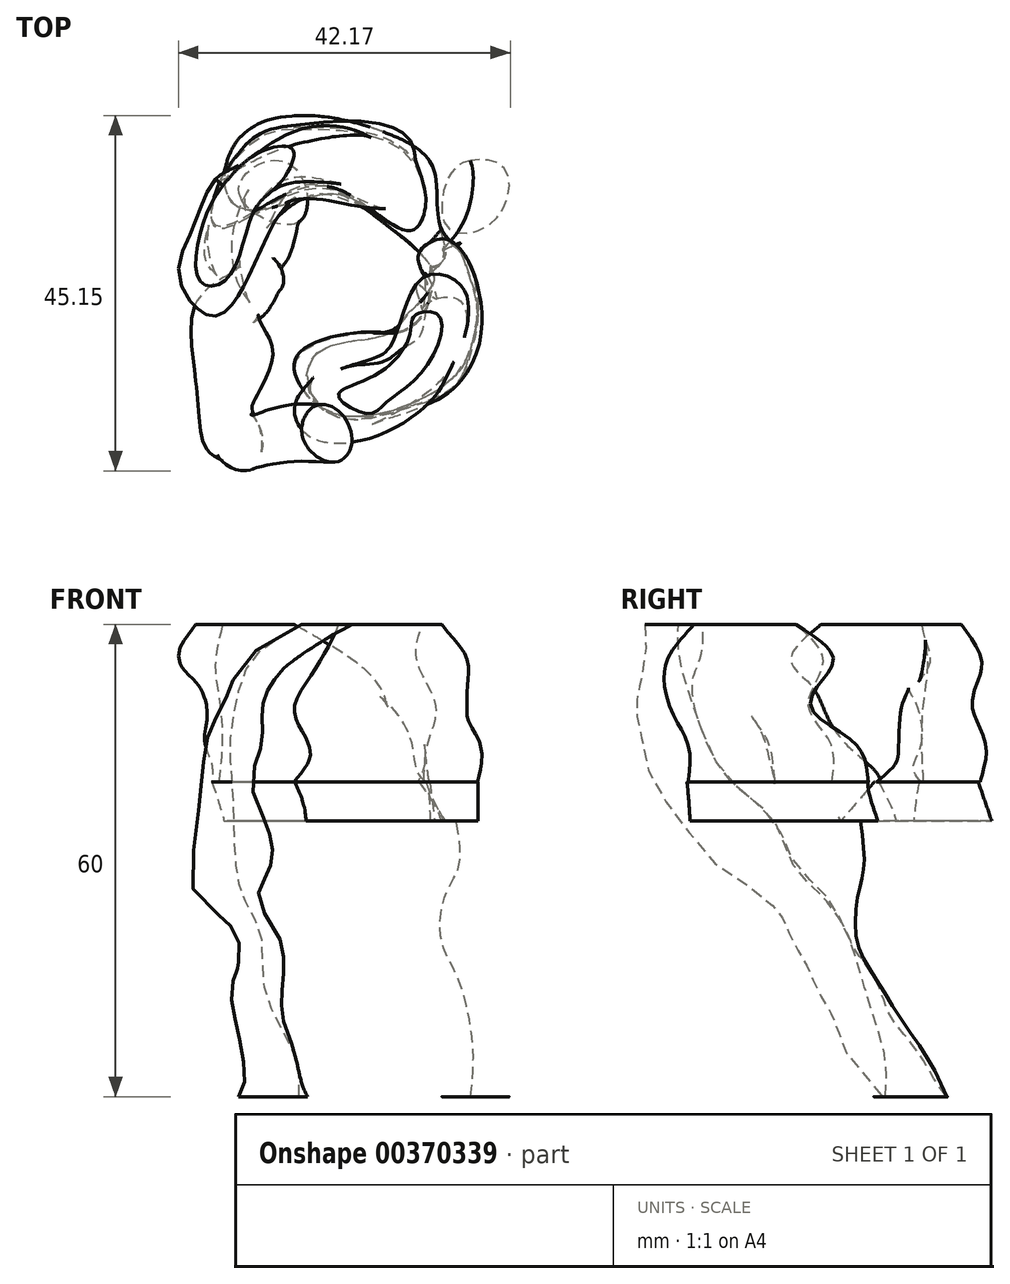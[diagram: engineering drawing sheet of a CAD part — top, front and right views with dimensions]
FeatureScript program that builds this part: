
annotation { "Feature Type Name" : "Feature", "Feature Type Description" : "" }
export const myFeature = defineFeature(function(context is Context, id is Id, definition is map)
    precondition{}
    {
        {
            var Q0;
            Q0=qCreatedBy(makeId("Top.planeOp"),FACE);
            cPlane(context, id + "F0", {"entities" : qUnion([Q0]), "cplaneType" : CPlaneType.OFFSET, "offset" : 5 * mm, "width" : 152.4 * mm, "height" : 152.4 * mm});
        }
        {
            var Q0;
            Q0=qCreatedBy(id+"F0.planeOp",FACE);
            var sketch = newSketch(context, id + "F1", { "sketchPlane" : qUnion([Q0])});
            skFitSpline(sketch, "E0", {"points": [v(-10.96, 11.92) * mm, v(-18.66, 15.77) * mm, v(-12.5, 19.43) * mm, v(-10.96, 11.92) * mm]});
            skSolve(sketch);
        }
        {
            var Q0;
            Q0=qCreatedBy(id+"F0.planeOp",FACE);
            var sketch = newSketch(context, id + "F2", { "sketchPlane" : qUnion([Q0])});
            skFitSpline(sketch, "E1", {"points": [v(10.8, 19.7) * mm, v(7.88, 17.32) * mm, v(7.93, 11.12) * mm, v(13.79, 12.03) * mm, v(15.2, 18.53) * mm, v(10.8, 19.7) * mm]});
            skSolve(sketch);
        }
        {
            var Q0;
            Q0=qCreatedBy(id+"F0.planeOp",FACE);
            cPlane(context, id + "F3", {"entities" : qUnion([Q0]), "cplaneType" : CPlaneType.OFFSET, "offset" : 5 * mm, "width" : 152.4 * mm, "height" : 152.4 * mm});
        }
        {
            var Q0;
            Q0=qCreatedBy(id+"F3.planeOp",FACE);
            var sketch = newSketch(context, id + "F4", { "sketchPlane" : qUnion([Q0])});
            skFitSpline(sketch, "E2", {"points": [v(-17.89, 12.12) * mm, v(-16.73, 16.35) * mm, v(-11.92, 13.66) * mm, v(-13.08, 7.3) * mm, v(-17.89, 12.12) * mm]});
            skSolve(sketch);
        }
        {
            var Q0;
            Q0=qCreatedBy(id+"F3.planeOp",FACE);
            var sketch = newSketch(context, id + "F5", { "sketchPlane" : qUnion([Q0])});
            skFitSpline(sketch, "E3", {"points": [v(13.6, 16.47) * mm, v(8.9, 16.15) * mm, v(7.47, 12.01) * mm, v(9.86, 7.3) * mm, v(14.84, 7.32) * mm, v(13.6, 16.47) * mm]});
            skSolve(sketch);
        }
        {
            var Q0;
            Q0=qCreatedBy(id+"F3.planeOp",FACE);
            cPlane(context, id + "F6", {"entities" : qUnion([Q0]), "cplaneType" : CPlaneType.OFFSET, "offset" : 5 * mm, "width" : 152.4 * mm, "height" : 152.4 * mm});
        }
        {
            var Q0;
            Q0=qCreatedBy(id+"F6.planeOp",FACE);
            var sketch = newSketch(context, id + "F7", { "sketchPlane" : qUnion([Q0])});
            skFitSpline(sketch, "E4", {"points": [v(-18.08, 9.04) * mm, v(-18.85, 12.3) * mm, v(-14.42, 11.16) * mm, v(-13.66, 5.39) * mm, v(-18.08, 9.04) * mm]});
            skSolve(sketch);
        }
        {
            var Q0;
            Q0=qCreatedBy(id+"F6.planeOp",FACE);
            var sketch = newSketch(context, id + "F8", { "sketchPlane" : qUnion([Q0])});
            skFitSpline(sketch, "E5", {"points": [v(10.24, 13.8) * mm, v(6.16, 10.54) * mm, v(7.66, 5.82) * mm, v(13.24, 4.66) * mm, v(13.5, 10.57) * mm, v(10.24, 13.8) * mm]});
            skSolve(sketch);
        }
        {
            var Q0;
            Q0=qCreatedBy(id+"F6.planeOp",FACE);
            cPlane(context, id + "F9", {"entities" : qUnion([Q0]), "cplaneType" : CPlaneType.OFFSET, "offset" : 5 * mm, "width" : 152.4 * mm, "height" : 152.4 * mm});
        }
        {
            var Q0;
            Q0=qCreatedBy(id+"F9.planeOp",FACE);
            var sketch = newSketch(context, id + "F10", { "sketchPlane" : qUnion([Q0])});
            skFitSpline(sketch, "E6", {"points": [v(-19.23, 7.7) * mm, v(-17.89, 10.58) * mm, v(-13.08, 3.85) * mm, v(-17.89, 3.27) * mm, v(-19.23, 7.7) * mm]});
            skSolve(sketch);
        }
        {
            var Q0;
            Q0=qCreatedBy(id+"F9.planeOp",FACE);
            var sketch = newSketch(context, id + "F11", { "sketchPlane" : qUnion([Q0])});
            skFitSpline(sketch, "E7", {"points": [v(8.32, 10.92) * mm, v(5.05, 8.14) * mm, v(7.28, 3.19) * mm, v(11.85, 3.4) * mm, v(12, 7.44) * mm, v(8.32, 10.92) * mm]});
            skSolve(sketch);
        }
        {
            var Q0;
            Q0=qCreatedBy(id+"F9.planeOp",FACE);
            cPlane(context, id + "F12", {"entities" : qUnion([Q0]), "cplaneType" : CPlaneType.OFFSET, "offset" : 5 * mm, "width" : 152.4 * mm, "height" : 152.4 * mm});
        }
        {
            var Q0;
            Q0=qCreatedBy(id+"F12.planeOp",FACE);
            var sketch = newSketch(context, id + "F13", { "sketchPlane" : qUnion([Q0])});
            skFitSpline(sketch, "E8", {"points": [v(-18.29, 6.81) * mm, v(-18.45, 4.24) * mm, v(-16.23, 0) * mm, v(-13.87, 2.6) * mm, v(-14.27, 6.83) * mm, v(-18.29, 6.81) * mm]});
            skSolve(sketch);
        }
        {
            var Q0;
            Q0=qCreatedBy(id+"F12.planeOp",FACE);
            var sketch = newSketch(context, id + "F14", { "sketchPlane" : qUnion([Q0])});
            skFitSpline(sketch, "E9", {"points": [v(7.64, 7.65) * mm, v(3.8, 9.66) * mm, v(0, 9.46) * mm, v(-2.02, 4.86) * mm, v(0, 0) * mm, v(9.54, 0) * mm, v(7.64, 7.65) * mm]});
            skSolve(sketch);
        }
        {
            var Q0;
            Q0=qCreatedBy(id+"F12.planeOp",FACE);
            cPlane(context, id + "F15", {"entities" : qUnion([Q0]), "cplaneType" : CPlaneType.OFFSET, "offset" : 5 * mm, "width" : 152.4 * mm, "height" : 152.4 * mm});
        }
        {
            var Q0;
            Q0=qCreatedBy(id+"F15.planeOp",FACE);
            var sketch = newSketch(context, id + "F16", { "sketchPlane" : qUnion([Q0])});
            skFitSpline(sketch, "E10", {"points": [v(-18.6, 4.65) * mm, v(-22.98, 2.98) * mm, v(-23.13, 0) * mm, v(-19.28, -3.26) * mm, v(-16.2, 0) * mm, v(-18.6, 4.65) * mm]});
            skSolve(sketch);
        }
        {
            var Q0;
            Q0=qCreatedBy(id+"F15.planeOp",FACE);
            var sketch = newSketch(context, id + "F17", { "sketchPlane" : qUnion([Q0])});
            skFitSpline(sketch, "E11", {"points": [v(7.68, 6.97) * mm, v(5.25, 13.94) * mm, v(-1.9, 16.67) * mm, v(-3.69, 12.07) * mm, v(-3.1, 6.74) * mm, v(0, -1.34) * mm, v(-2.44, -7.79) * mm, v(7.07, -8.48) * mm, v(9.93, 0) * mm, v(7.68, 6.97) * mm]});
            skSolve(sketch);
        }
        {
            var Q0;
            Q0=qCreatedBy(id+"F15.planeOp",FACE);
            cPlane(context, id + "F18", {"entities" : qUnion([Q0]), "cplaneType" : CPlaneType.OFFSET, "offset" : 5 * mm, "width" : 152.4 * mm, "height" : 152.4 * mm});
        }
        {
            var Q0;
            Q0=qCreatedBy(id+"F18.planeOp",FACE);
            var sketch = newSketch(context, id + "F19", { "sketchPlane" : qUnion([Q0])});
            skFitSpline(sketch, "E12", {"points": [v(-22.76, 0) * mm, v(-24.55, -3.05) * mm, v(-21.94, -10.02) * mm, v(-14.84, -5.95) * mm, v(-15.97, -1.54) * mm, v(-22.76, 0) * mm]});
            skSolve(sketch);
        }
        {
            var Q0;
            Q0=qCreatedBy(id+"F18.planeOp",FACE);
            var sketch = newSketch(context, id + "F20", { "sketchPlane" : qUnion([Q0])});
            skFitSpline(sketch, "E13", {"points": [v(3.97, 18.59) * mm, v(0, 21.33) * mm, v(-10.87, 23.3) * mm, v(-10.82, 17.6) * mm, v(-4.03, 12.67) * mm, v(0, 7.72) * mm, v(3.38, 0) * mm, v(0, -4.6) * mm, v(-5.9, -5.91) * mm, v(-8.42, -10.34) * mm, v(0, -12.51) * mm, v(10.7, -2.54) * mm, v(9.52, 9.05) * mm, v(3.97, 18.59) * mm]});
            skSolve(sketch);
        }
        {
            var Q0;
            Q0=qCreatedBy(id+"F18.planeOp",FACE);
            cPlane(context, id + "F21", {"entities" : qUnion([Q0]), "cplaneType" : CPlaneType.OFFSET, "offset" : 5 * mm, "width" : 152.4 * mm, "height" : 152.4 * mm});
        }
        {
            var Q0;
            Q0=qCreatedBy(id+"F21.planeOp",FACE);
            var sketch = newSketch(context, id + "F22", { "sketchPlane" : qUnion([Q0])});
            skFitSpline(sketch, "E14", {"points": [v(-21.05, -2.61) * mm, v(-23.57, -7.6) * mm, v(-22.98, -13.47) * mm, v(-18.96, -13.09) * mm, v(-15.36, -6.64) * mm, v(-17.95, -2.6) * mm, v(-21.05, -2.61) * mm]});
            skSolve(sketch);
        }
        {
            var Q0;
            Q0=qCreatedBy(id+"F21.planeOp",FACE);
            var sketch = newSketch(context, id + "F23", { "sketchPlane" : qUnion([Q0])});
            skFitSpline(sketch, "E15", {"points": [v(0, 23.21) * mm, v(-9.58, 25.38) * mm, v(-18.32, 22.77) * mm, v(-20.28, 15.78) * mm, v(-16.6, 13.4) * mm, v(-6.58, 15.47) * mm, v(0, 11.63) * mm, v(6.11, 4.85) * mm, v(2.68, 0) * mm, v(0, -2.53) * mm, v(-9.16, -5.14) * mm, v(-7.83, -11.94) * mm, v(6.04, -9.86) * mm, v(11.1, -3.22) * mm, v(10.66, 6.52) * mm, v(6.97, 11.3) * mm, v(6, 18.83) * mm, v(0, 23.21) * mm]});
            skSolve(sketch);
        }
        {
            var Q0;
            Q0=qCreatedBy(id+"F21.planeOp",FACE);
            var sketch = newSketch(context, id + "F24", { "sketchPlane" : qUnion([Q0])});
            skFitSpline(sketch, "E16", {"points": [v(-18.3, 22.81) * mm, v(-19.22, 21.67) * mm, v(-20.07, 19.82) * mm, v(-20.41, 18.4) * mm, v(-20.5, 16.83) * mm, v(-20.25, 15.7) * mm, v(-19.75, 14.64) * mm, v(-18.75, 13.82) * mm, v(-17.3, 13.37) * mm, v(-16.55, 13.34) * mm, v(-13.48, 13.95) * mm, v(-11.7, 14.42) * mm, v(-8.93, 15.2) * mm, v(-6.36, 15.48) * mm, v(-4.09, 14.8) * mm, v(-1.52, 12.84) * mm, v(0.94, 10.85) * mm, v(3.75, 8.6) * mm, v(5.6, 6.49) * mm, v(5.84, 6.25) * mm, v(6.31, 6.3) * mm, v(7.32, 7.2) * mm, v(6.95, 11.33) * mm, v(6.79, 11.88) * mm, v(6.58, 13.68) * mm, v(6.4, 17.39) * mm, v(6.02, 18.8) * mm, v(5.52, 19.7) * mm, v(4.49, 20.85) * mm, v(2.87, 21.89) * mm, v(-1.36, 23.71) * mm, v(-6.76, 25.11) * mm, v(-9.51, 25.4) * mm, v(-13.5, 25.17) * mm, v(-15.39, 24.67) * mm, v(-16.79, 24) * mm, v(-18.3, 22.81) * mm]});
            skSolve(sketch);
        }
        {
            var Q0;
            Q0=qCreatedBy(id+"F21.planeOp",FACE);
            var sketch = newSketch(context, id + "F25", { "sketchPlane" : qUnion([Q0])});
            skFitSpline(sketch, "E17", {"points": [v(7.1, 6.72) * mm, v(7.57, 7.44) * mm, v(7.48, 9.22) * mm, v(7.04, 10.95) * mm, v(7.43, 10.37) * mm, v(8.43, 9.03) * mm, v(9.5, 8.16) * mm, v(10.74, 6.48) * mm, v(11.65, 3.65) * mm, v(11.7, 2.07) * mm, v(11.75, 0.63) * mm, v(11.4, -1.67) * mm, v(11.07, -3.2) * mm, v(10.35, -5.6) * mm, v(9.3, -7.1) * mm, v(7.9, -8.53) * mm, v(6.28, -9.78) * mm, v(4.45, -10.64) * mm, v(1.77, -11.8) * mm, v(-3.17, -12.9) * mm, v(-6.49, -12.56) * mm, v(-7.83, -11.9) * mm, v(-9.41, -10.26) * mm, v(-10.08, -7.72) * mm, v(-9.5, -5.75) * mm, v(-8.98, -4.98) * mm, v(-7.54, -4.07) * mm, v(-5.24, -3.4) * mm, v(-1.69, -2.92) * mm, v(0, -2.49) * mm, v(1.43, -1.77) * mm, v(2.58, 0) * mm, v(3.93, 1.2) * mm, v(5.03, 2.45) * mm, v(5.9, 3.85) * mm, v(6.18, 5.04) * mm, v(5.65, 6.15) * mm, v(6.47, 6.15) * mm, v(7.1, 6.72) * mm]});
            skSolve(sketch);
        }
        {
            var Q0;
            Q0=qCreatedBy(id+"F21.planeOp",FACE);
            cPlane(context, id + "F26", {"entities" : qUnion([Q0]), "cplaneType" : CPlaneType.OFFSET, "offset" : 5 * mm, "width" : 152.4 * mm, "height" : 152.4 * mm});
        }
        {
            var Q0;
            Q0=qCreatedBy(id+"F26.planeOp",FACE);
            var sketch = newSketch(context, id + "F27", { "sketchPlane" : qUnion([Q0])});
            skFitSpline(sketch, "E18", {"points": [v(-19.34, -7.7) * mm, v(-23.14, -12.32) * mm, v(-21.82, -17.65) * mm, v(-17.1, -13.03) * mm, v(-19.34, -7.7) * mm]});
            skSolve(sketch);
        }
        {
            var Q0;
            Q0=qCreatedBy(id+"F26.planeOp",FACE);
            var sketch = newSketch(context, id + "F28", { "sketchPlane" : qUnion([Q0])});
            skFitSpline(sketch, "E19", {"points": [v(4.96, 4.98) * mm, v(4.39, 7.92) * mm, v(7.84, 9.58) * mm, v(10.62, 5.18) * mm, v(11.75, -0.1) * mm, v(10.88, -4.38) * mm, v(8.9, -8.98) * mm, v(2.16, -11.95) * mm, v(-5.68, -13.09) * mm, v(-11.01, -8.51) * mm, v(-10.86, -4.83) * mm, v(-2.84, -2.23) * mm, v(2.63, -1.84) * mm, v(5.53, 1.67) * mm, v(4.96, 4.98) * mm]});
            skSolve(sketch);
        }
        {
            var Q0;
            Q0=qCreatedBy(id+"F26.planeOp",FACE);
            var sketch = newSketch(context, id + "F29", { "sketchPlane" : qUnion([Q0])});
            skFitSpline(sketch, "E20", {"points": [v(-21.15, 16.47) * mm, v(-15.53, 22.93) * mm, v(-11.34, 23.68) * mm, v(-3.11, 23.16) * mm, v(3.12, 20.06) * mm, v(4.98, 15.65) * mm, v(5, 13.08) * mm, v(3.2, 10.5) * mm, v(-4.88, 15.25) * mm, v(-10.18, 15.96) * mm, v(-15.28, 13.73) * mm, v(-21.47, 11.13) * mm, v(-21.15, 16.47) * mm]});
            skSolve(sketch);
        }
        {
            var Q0;
            Q0=qCreatedBy(id+"F26.planeOp",FACE);
            var sketch = newSketch(context, id + "F30", { "sketchPlane" : qUnion([Q0])});
            skFitSpline(sketch, "E21", {"points": [v(-21.17, 16.74) * mm, v(-15.56, 23.2) * mm, v(-11.36, 23.96) * mm, v(-3.14, 23.44) * mm, v(3.1, 20.34) * mm, v(4.96, 15.93) * mm, v(4.98, 13.35) * mm, v(3.17, 10.77) * mm, v(-4.9, 15.52) * mm, v(-10.2, 16.24) * mm, v(-15.3, 14) * mm, v(-21.5, 11.4) * mm, v(-21.17, 16.74) * mm]});
            skSolve(sketch);
        }
        {
            var Q0;
            Q0=qCreatedBy(id+"F26.planeOp",FACE);
            var sketch = newSketch(context, id + "F31", { "sketchPlane" : qUnion([Q0])});
            skFitSpline(sketch, "E22", {"points": [v(4.86, 5.08) * mm, v(4.29, 8.02) * mm, v(7.75, 9.69) * mm, v(10.52, 5.29) * mm, v(11.65, 0) * mm, v(10.78, -4.28) * mm, v(8.8, -8.88) * mm, v(2.07, -11.85) * mm, v(-5.78, -12.99) * mm, v(-11.11, -8.41) * mm, v(-10.96, -4.73) * mm, v(-2.94, -2.13) * mm, v(2.54, -1.74) * mm, v(5.43, 1.77) * mm, v(4.86, 5.08) * mm]});
            skSolve(sketch);
        }
        {
            var Q0;
            Q0=qCreatedBy(id+"F26.planeOp",FACE);
            cPlane(context, id + "F32", {"entities" : qUnion([Q0]), "cplaneType" : CPlaneType.OFFSET, "offset" : 5 * mm, "width" : 152.4 * mm, "height" : 152.4 * mm});
        }
        {
            var Q0;
            Q0=qCreatedBy(id+"F32.planeOp",FACE);
            var sketch = newSketch(context, id + "F33", { "sketchPlane" : qUnion([Q0])});
            skFitSpline(sketch, "E23", {"points": [v(-22.74, -13.37) * mm, v(-19.83, -10.79) * mm, v(-16.16, -13.9) * mm, v(-16.49, -17.95) * mm, v(-20.5, -18.51) * mm, v(-22.74, -13.37) * mm]});
            skSolve(sketch);
        }
        {
            var Q0;
            Q0=qCreatedBy(id+"F32.planeOp",FACE);
            var sketch = newSketch(context, id + "F34", { "sketchPlane" : qUnion([Q0])});
            skFitSpline(sketch, "E24", {"points": [v(-17.16, 21.77) * mm, v(-20.23, 17.53) * mm, v(-21.85, 13.48) * mm, v(-22.71, 7.22) * mm, v(-19.6, 7.24) * mm, v(-14.17, 12.4) * mm, v(-10.9, 16.28) * mm, v(-3.96, 15.02) * mm, v(0, 13.76) * mm, v(3.31, 20.39) * mm, v(0, 24.04) * mm, v(-8.96, 24.2) * mm, v(-17.16, 21.77) * mm]});
            skSolve(sketch);
        }
        {
            var Q0;
            Q0=qCreatedBy(id+"F32.planeOp",FACE);
            var sketch = newSketch(context, id + "F35", { "sketchPlane" : qUnion([Q0])});
            skFitSpline(sketch, "E25", {"points": [v(4.04, -2.97) * mm, v(-3.63, -3) * mm, v(-8.36, -6.33) * mm, v(-9.41, -11.85) * mm, v(1.55, -12.54) * mm, v(10.1, -7.36) * mm, v(11.67, 2.4) * mm, v(8.16, 7.9) * mm, v(5.08, 3.66) * mm, v(4.04, -2.97) * mm]});
            skSolve(sketch);
        }
        {
            var Q0;
            Q0=qCreatedBy(id+"F32.planeOp",FACE);
            cPlane(context, id + "F36", {"entities" : qUnion([Q0]), "cplaneType" : CPlaneType.OFFSET, "offset" : 5 * mm, "width" : 152.4 * mm, "height" : 152.4 * mm});
        }
        {
            var Q0;
            Q0=qCreatedBy(id+"F36.planeOp",FACE);
            var sketch = newSketch(context, id + "F37", { "sketchPlane" : qUnion([Q0])});
            skFitSpline(sketch, "E26", {"points": [v(-20.17, -13.68) * mm, v(-17.44, -12.48) * mm, v(-15.9, -14.19) * mm, v(-16.24, -18.98) * mm, v(-19.32, -19.15) * mm, v(-20.17, -13.68) * mm]});
            skSolve(sketch);
        }
        {
            var Q0;
            Q0=qCreatedBy(id+"F36.planeOp",FACE);
            var sketch = newSketch(context, id + "F38", { "sketchPlane" : qUnion([Q0])});
            skFitSpline(sketch, "E27", {"points": [v(-22.5, 7.64) * mm, v(-22.19, 14.45) * mm, v(-18.2, 19.43) * mm, v(-10.37, 22.03) * mm, v(-2.52, 22.8) * mm, v(0, 21.16) * mm, v(0, 17.67) * mm, v(0, 15.08) * mm, v(-5.75, 14.33) * mm, v(-9.78, 15.78) * mm, v(-12.69, 13.93) * mm, v(-14.85, 10.8) * mm, v(-17.2, 6) * mm, v(-20.28, 3.79) * mm, v(-22.5, 7.64) * mm]});
            skSolve(sketch);
        }
        {
            var Q0;
            Q0=qCreatedBy(id+"F36.planeOp",FACE);
            var sketch = newSketch(context, id + "F39", { "sketchPlane" : qUnion([Q0])});
            skFitSpline(sketch, "E28", {"points": [v(-4.85, -6.27) * mm, v(0, -5.7) * mm, v(2.25, -3.12) * mm, v(5.13, 1.48) * mm, v(9.52, 1.86) * mm, v(10.1, -2.36) * mm, v(7.6, -7.69) * mm, v(0, -13.04) * mm, v(-9.16, -15.46) * mm, v(-11.39, -11.61) * mm, v(-4.85, -6.27) * mm]});
            skSolve(sketch);
        }
        {
            var Q0;
            Q0=qCreatedBy(id+"F36.planeOp",FACE);
            cPlane(context, id + "F40", {"entities" : qUnion([Q0]), "cplaneType" : CPlaneType.OFFSET, "offset" : 5 * mm, "width" : 152.4 * mm, "height" : 152.4 * mm});
        }
        {
            var Q0;
            Q0=qCreatedBy(id+"F40.planeOp",FACE);
            var sketch = newSketch(context, id + "F41", { "sketchPlane" : qUnion([Q0])});
            skFitSpline(sketch, "E29", {"points": [v(-17.43, 19.3) * mm, v(-21.43, 17.44) * mm, v(-24.66, 10.46) * mm, v(-25.88, 4.04) * mm, v(-21.46, 0) * mm, v(-18.57, 4.07) * mm, v(-17.16, 10.3) * mm, v(-14.28, 14.54) * mm, v(-9.73, 17.5) * mm, v(-4.6, 16.96) * mm, v(-4.3, 22.65) * mm, v(-10.7, 23.54) * mm, v(-17.43, 19.3) * mm]});
            skSolve(sketch);
        }
        {
            var Q0;
            Q0=qCreatedBy(id+"F40.planeOp",FACE);
            var sketch = newSketch(context, id + "F42", { "sketchPlane" : qUnion([Q0])});
            skFitSpline(sketch, "E30", {"points": [v(-3.12, -5.96) * mm, v(-7.12, -8.18) * mm, v(-8.16, -14.24) * mm, v(-3.2, -15.87) * mm, v(5.34, -11.25) * mm, v(8.4, -6.28) * mm, v(10.15, 2.9) * mm, v(5.56, 5.08) * mm, v(2.13, 0) * mm, v(0, -4.67) * mm, v(-3.12, -5.96) * mm]});
            skSolve(sketch);
        }
        {
            var Q0;
            Q0=qCreatedBy(id+"F40.planeOp",FACE);
            var sketch = newSketch(context, id + "F43", { "sketchPlane" : qUnion([Q0])});
            skFitSpline(sketch, "E31", {"points": [v(-16.93, -13.68) * mm, v(-15.73, -12.3) * mm, v(-13, -12.14) * mm, v(-12.3, -15.22) * mm, v(-13, -18.63) * mm, v(-18.12, -16.07) * mm, v(-16.93, -13.68) * mm]});
            skSolve(sketch);
        }
        {
            var Q0;
            Q0=qCreatedBy(id+"F40.planeOp",FACE);
            cPlane(context, id + "F44", {"entities" : qUnion([Q0]), "cplaneType" : CPlaneType.OFFSET, "offset" : 5 * mm, "width" : 152.4 * mm, "height" : 152.4 * mm});
        }
        {
            var Q0;
            Q0=qCreatedBy(id+"F44.planeOp",FACE);
            var sketch = newSketch(context, id + "F45", { "sketchPlane" : qUnion([Q0])});
            skFitSpline(sketch, "E32", {"points": [v(-19.84, 17.5) * mm, v(-22.83, 12.63) * mm, v(-23.58, 4.4) * mm, v(-20.21, 4.59) * mm, v(-16.66, 13.38) * mm, v(-13.48, 16.75) * mm, v(-11.8, 21.06) * mm, v(-15.72, 20.87) * mm, v(-19.84, 17.5) * mm]});
            skSolve(sketch);
        }
        {
            var Q0;
            Q0=qCreatedBy(id+"F44.planeOp",FACE);
            var sketch = newSketch(context, id + "F46", { "sketchPlane" : qUnion([Q0])});
            skFitSpline(sketch, "E33", {"points": [v(3, -2.71) * mm, v(-1.68, -7.77) * mm, v(-5.99, -10.2) * mm, v(-2.25, -12.45) * mm, v(0, -11.14) * mm, v(5.05, -6.64) * mm, v(6.74, 0) * mm, v(3.74, 0) * mm, v(3, -2.71) * mm]});
            skSolve(sketch);
        }
        {
            var Q0;
            Q0=qCreatedBy(id+"F44.planeOp",FACE);
            var sketch = newSketch(context, id + "F47", { "sketchPlane" : qUnion([Q0])});
            skFitSpline(sketch, "E34", {"points": [v(-10.6, -15.22) * mm, v(-8.9, -11.45) * mm, v(-5.47, -12.65) * mm, v(-4.45, -16.93) * mm, v(-7, -18.63) * mm, v(-10.6, -15.22) * mm]});
            skSolve(sketch);
        }
        {
            var Q0;
            Q0=qSketchRegion(id+"F1",true);
            var Q1;
            Q1=qSketchRegion(id+"F4",true);
            var Q2;
            Q2=qSketchRegion(id+"F7",true);
            var Q3;
            Q3=qSketchRegion(id+"F10",true);
            var Q4;
            Q4=qSketchRegion(id+"F13",true);
            var Q5;
            Q5=qSketchRegion(id+"F16",true);
            var Q6;
            Q6=qSketchRegion(id+"F19",true);
            var Q7;
            Q7=qSketchRegion(id+"F22",true);
            var Q8;
            Q8=qSketchRegion(id+"F27",true);
            var Q9;
            Q9=qSketchRegion(id+"F33",true);
            var Q10;
            Q10=qSketchRegion(id+"F37",true);
            var Q11;
            Q11=qSketchRegion(id+"F43",true);
            var Q12;
            Q12=qSketchRegion(id+"F47",true);
            loft(context, id + "F48", {"sheetProfilesArray" : [{ "sheetProfileEntities" : qUnion([Q0]) }, { "sheetProfileEntities" : qUnion([Q1]) }, { "sheetProfileEntities" : qUnion([Q2]) }, { "sheetProfileEntities" : qUnion([Q3]) }, { "sheetProfileEntities" : qUnion([Q4]) }, { "sheetProfileEntities" : qUnion([Q5]) }, { "sheetProfileEntities" : qUnion([Q6]) }, { "sheetProfileEntities" : qUnion([Q7]) }, { "sheetProfileEntities" : qUnion([Q8]) }, { "sheetProfileEntities" : qUnion([Q9]) }, { "sheetProfileEntities" : qUnion([Q10]) }, { "sheetProfileEntities" : qUnion([Q11]) }, { "sheetProfileEntities" : qUnion([Q12]) }]});
        }
        {
            var Q0;
            Q0=qSketchRegion(id+"F2",true);
            var Q1;
            Q1=qSketchRegion(id+"F5",true);
            var Q2;
            Q2=qSketchRegion(id+"F8",true);
            var Q3;
            Q3=qSketchRegion(id+"F11",true);
            var Q4;
            Q4=qSketchRegion(id+"F14",true);
            var Q5;
            Q5=qSketchRegion(id+"F17",true);
            var Q6;
            Q6=qSketchRegion(id+"F20",true);
            var Q7;
            Q7=qSketchRegion(id+"F23",true);
            loft(context, id + "F49", {"sheetProfilesArray" : [{ "sheetProfileEntities" : qUnion([Q0]) }, { "sheetProfileEntities" : qUnion([Q1]) }, { "sheetProfileEntities" : qUnion([Q2]) }, { "sheetProfileEntities" : qUnion([Q3]) }, { "sheetProfileEntities" : qUnion([Q4]) }, { "sheetProfileEntities" : qUnion([Q5]) }, { "sheetProfileEntities" : qUnion([Q6]) }, { "sheetProfileEntities" : qUnion([Q7]) }]});
        }
        {
            var Q0;
            Q0=qSketchRegion(id+"F30",true);
            var Q1;
            Q1=qSketchRegion(id+"F34",true);
            var Q2;
            Q2=qSketchRegion(id+"F38",true);
            var Q3;
            Q3=qSketchRegion(id+"F41",true);
            var Q4;
            Q4=qSketchRegion(id+"F45",true);
            loft(context, id + "F50", {"sheetProfilesArray" : [{ "sheetProfileEntities" : qUnion([Q0]) }, { "sheetProfileEntities" : qUnion([Q1]) }, { "sheetProfileEntities" : qUnion([Q2]) }, { "sheetProfileEntities" : qUnion([Q3]) }, { "sheetProfileEntities" : qUnion([Q4]) }]});
        }
        {
            var Q0;
            Q0=qSketchRegion(id+"F31",true);
            var Q1;
            Q1=qSketchRegion(id+"F35",true);
            var Q2;
            Q2=qSketchRegion(id+"F39",true);
            var Q3;
            Q3=qSketchRegion(id+"F42",true);
            var Q4;
            Q4=qSketchRegion(id+"F46",true);
            loft(context, id + "F51", {"sheetProfilesArray" : [{ "sheetProfileEntities" : qUnion([Q0]) }, { "sheetProfileEntities" : qUnion([Q1]) }, { "sheetProfileEntities" : qUnion([Q2]) }, { "sheetProfileEntities" : qUnion([Q3]) }, { "sheetProfileEntities" : qUnion([Q4]) }]});
        }
        {
            var Q0;
            Q0=qSketchRegion(id+"F24",true);
            var Q1;
            Q1=qSketchRegion(id+"F29",true);
            loft(context, id + "F52", {"sheetProfilesArray" : [{ "sheetProfileEntities" : qUnion([Q0]) }, { "sheetProfileEntities" : qUnion([Q1]) }]});
        }
        {
            var Q0;
            Q0=qSketchRegion(id+"F25",true);
            var Q1;
            Q1=qSketchRegion(id+"F28",true);
            loft(context, id + "F53", {"sheetProfilesArray" : [{ "sheetProfileEntities" : qUnion([Q0]) }, { "sheetProfileEntities" : qUnion([Q1]) }]});
        }
    });
